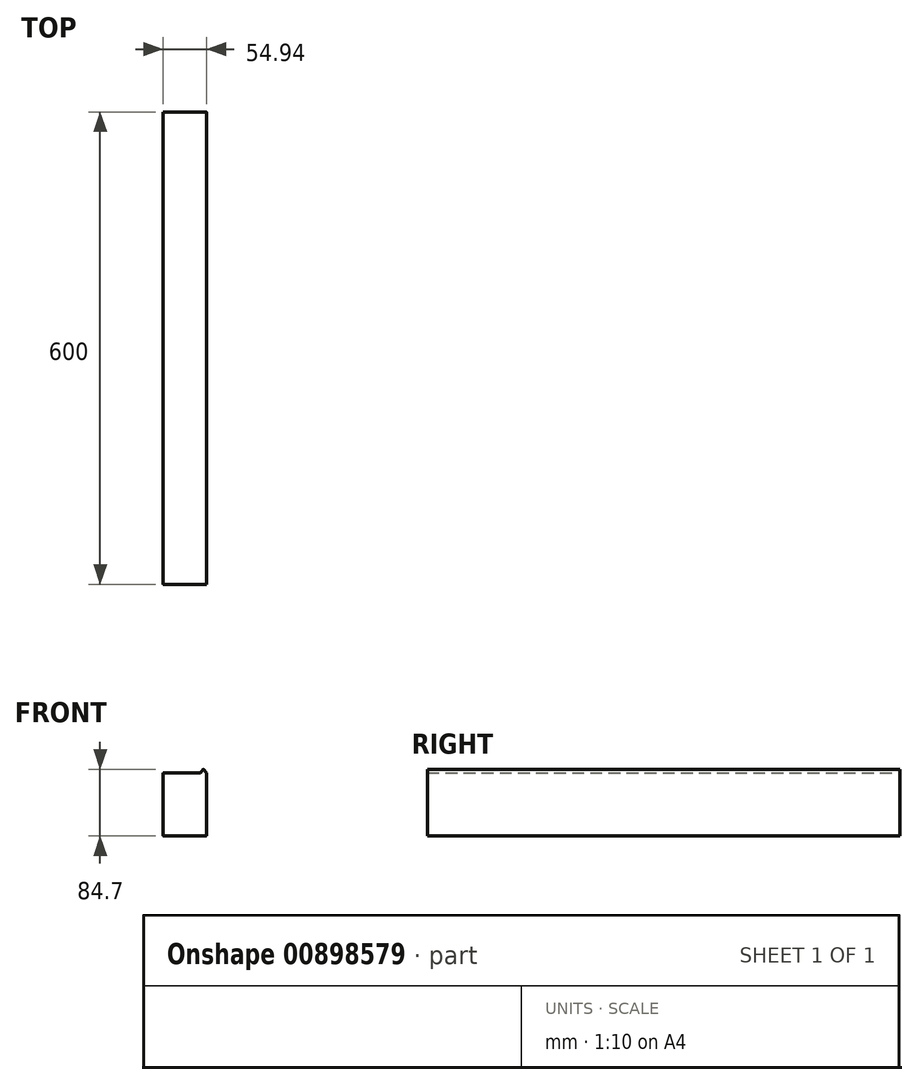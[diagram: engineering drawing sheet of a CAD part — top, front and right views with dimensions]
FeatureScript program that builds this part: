
annotation { "Feature Type Name" : "Feature", "Feature Type Description" : "" }
export const myFeature = defineFeature(function(context is Context, id is Id, definition is map)
    precondition{}
    {
        {
            var Q0;
            Q0=qCreatedBy(makeId("Front.planeOp"),FACE);
            var sketch = newSketch(context, id + "F0", { "sketchPlane" : qUnion([Q0])});
            skLineSegment(sketch, "E0.bottom", {"start": v(27.48, 40) * mm, "end": v(-27.48, 40) * mm});
            skLineSegment(sketch, "E0.top", {"start": v(27.48, -40) * mm, "end": v(-27.48, -40) * mm});
            skLineSegment(sketch, "E0.left", {"start": v(27.48, 40) * mm, "end": v(27.48, -40) * mm});
            skLineSegment(sketch, "E0.right", {"start": v(-27.47, 40) * mm, "end": v(-27.48, -40) * mm});
            skPoint(sketch, "E0.middle", {"position": v(0, 0) * mm});
            skLineSegment(sketch, "E1", {"start": v(27.47, 40) * mm, "end": v(23.47, 45) * mm});
            skLineSegment(sketch, "E2", {"start": v(23.48, 45) * mm, "end": v(19.48, 40) * mm});
            skSolve(sketch);
        }
        {
            var Q0;
            Q0 = qSketchRegion(id + "F0", true);
            extrude(context, id + "F1", {"entities" : qUnion([Q0]), "depth" : 600 * mm, "offsetDistance" : 25 * mm});
        }
        {
            var Q0;
            Q0=makeQuery(id+"F1.opExtrude","SWEPT_EDGE",EDGE,{"disambiguationData":[OSD([sQuery(id+"F0.wireOp",EDGE,"E1"),sQuery(id+"F0.wireOp",EDGE,"E2")])]});
            var Q1;
            Q1=makeQuery(id+"F1.opExtrude","SWEPT_EDGE",EDGE,{"disambiguationData":[OSD([sQuery(id+"F0.wireOp",EDGE,"E0.bottom"),sQuery(id+"F0.wireOp",EDGE,"E0.left"),sQuery(id+"F0.wireOp",EDGE,"E1")])]});
            var Q2;
            Q2=makeQuery(id+"F1.opExtrude","SWEPT_EDGE",EDGE,{"disambiguationData":[OSD([sQuery(id+"F0.wireOp",EDGE,"E0.bottom"),sQuery(id+"F0.wireOp",EDGE,"E2")])]});
            var Q3;
            Q3=makeQuery(id+"F1.opExtrude","SWEPT_EDGE",EDGE,{"disambiguationData":[OSD([sQuery(id+"F0.wireOp",EDGE,"E0.bottom"),sQuery(id+"F0.wireOp",EDGE,"E0.right")])]});
            var Q4;
            Q4=makeQuery(id+"F1.opExtrude","SWEPT_EDGE",EDGE,{"disambiguationData":[OSD([sQuery(id+"F0.wireOp",EDGE,"E0.top"),sQuery(id+"F0.wireOp",EDGE,"E0.right")])]});
            var Q5;
            Q5=makeQuery(id+"F1.opExtrude","SWEPT_EDGE",EDGE,{"disambiguationData":[OSD([sQuery(id+"F0.wireOp",EDGE,"E0.top"),sQuery(id+"F0.wireOp",EDGE,"E0.left")])]});
            fillet(context, id + "F2", {"entities" : qUnion([Q0, Q1, Q2, Q3, Q4, Q5]), "radius" : 0.5 * mm, "tangentPropagation" : true, "allowEdgeOverflow" : false});
        }
    });
